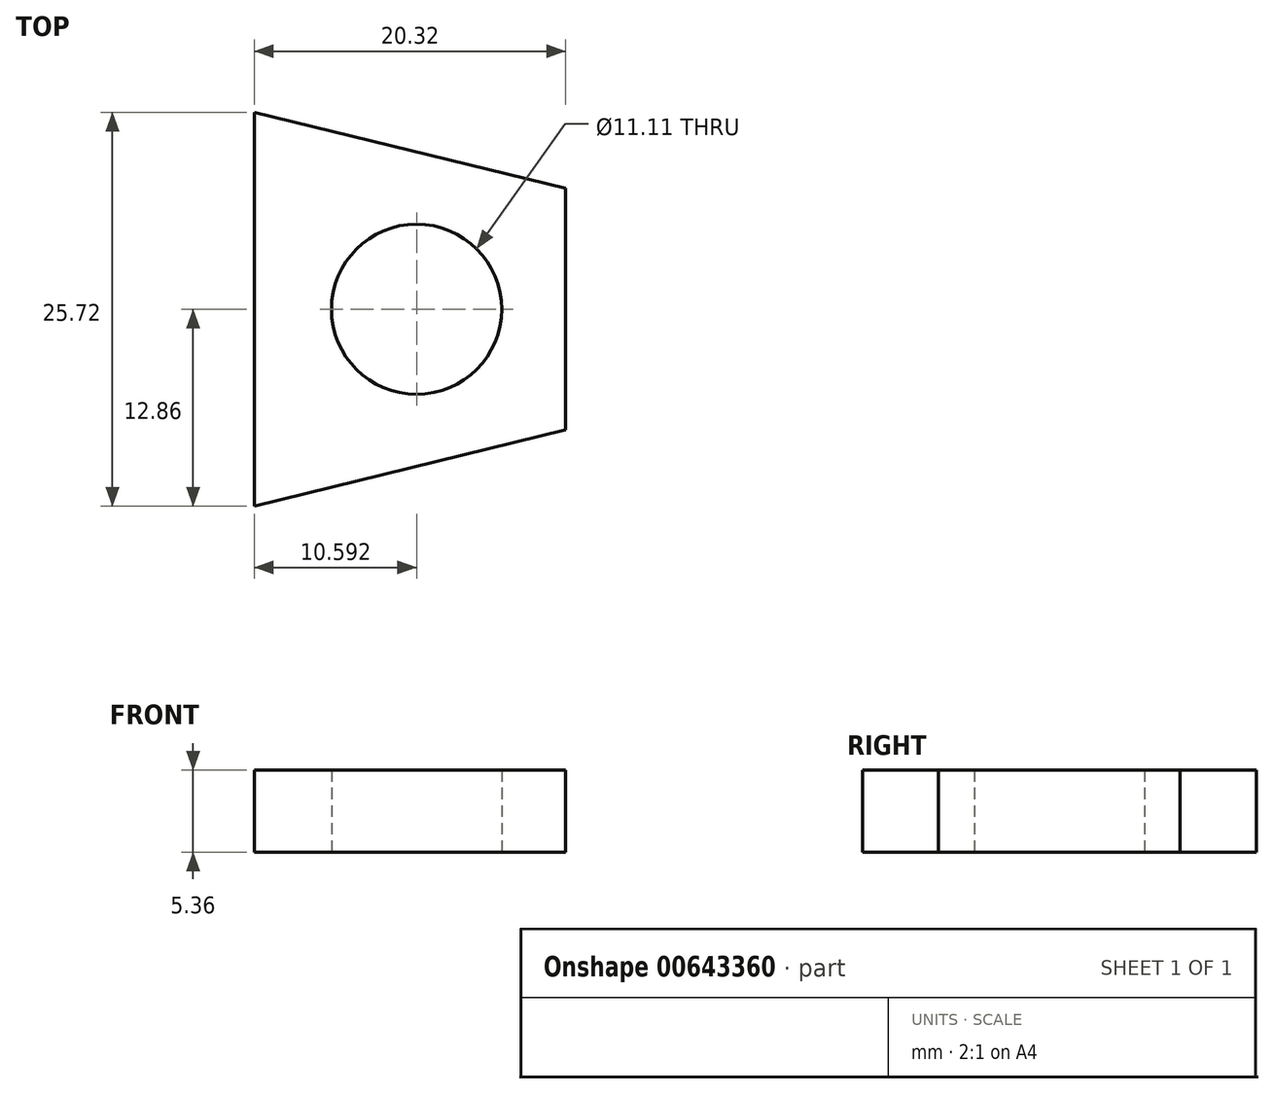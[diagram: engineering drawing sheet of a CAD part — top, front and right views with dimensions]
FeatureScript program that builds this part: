
annotation { "Feature Type Name" : "Feature", "Feature Type Description" : "" }
export const myFeature = defineFeature(function(context is Context, id is Id, definition is map)
    precondition{}
    {
        {
            var Q0;
            Q0=qCreatedBy(makeId("Top.planeOp"),FACE);
            var sketch = newSketch(context, id + "F0", { "sketchPlane" : qUnion([Q0])});
            skLineSegment(sketch, "E0", {"start": v(20.32, 0) * mm, "end": v(20.32, 7.89) * mm});
            skLineSegment(sketch, "E1", {"start": v(20.32, 7.89) * mm, "end": v(0, 12.86) * mm});
            skLineSegment(sketch, "E2", {"start": v(-10.94, 0) * mm, "end": v(0, 0) * mm, "construction": true});
            skLineSegment(sketch, "E3", {"start": v(0, 12.86) * mm, "end": v(0, 0) * mm});
            skCircle(sketch, "E4", {"center": v(10.6, 0) * mm, "radius": 5.56 * mm});
            skLineSegment(sketch, "E5.MirrorCS", {"start": v(0, -12.86) * mm, "end": v(0, 0) * mm});
            skLineSegment(sketch, "E6.MirrorCS", {"start": v(20.32, -7.89) * mm, "end": v(0, -12.86) * mm});
            skLineSegment(sketch, "E7.MirrorCS", {"start": v(20.32, 0) * mm, "end": v(20.32, -7.89) * mm});
            skSolve(sketch);
        }
        {
            var Q0;
            Q0=makeQuery(id+"F0.imprint","IMPRINT",FACE,{"disambiguationData":[TD([[makeQuery(id+"F0.imprint","IMPRINT",EDGE,{"derivedFrom":sQuery(id+"F0.wireOp",EDGE,"E0")}),1.0]])]});
            extrude(context, id + "F1", {"entities" : qUnion([Q0]), "depth" : 5.36 * mm, "offsetDistance" : 25.4 * mm});
        }
    });
